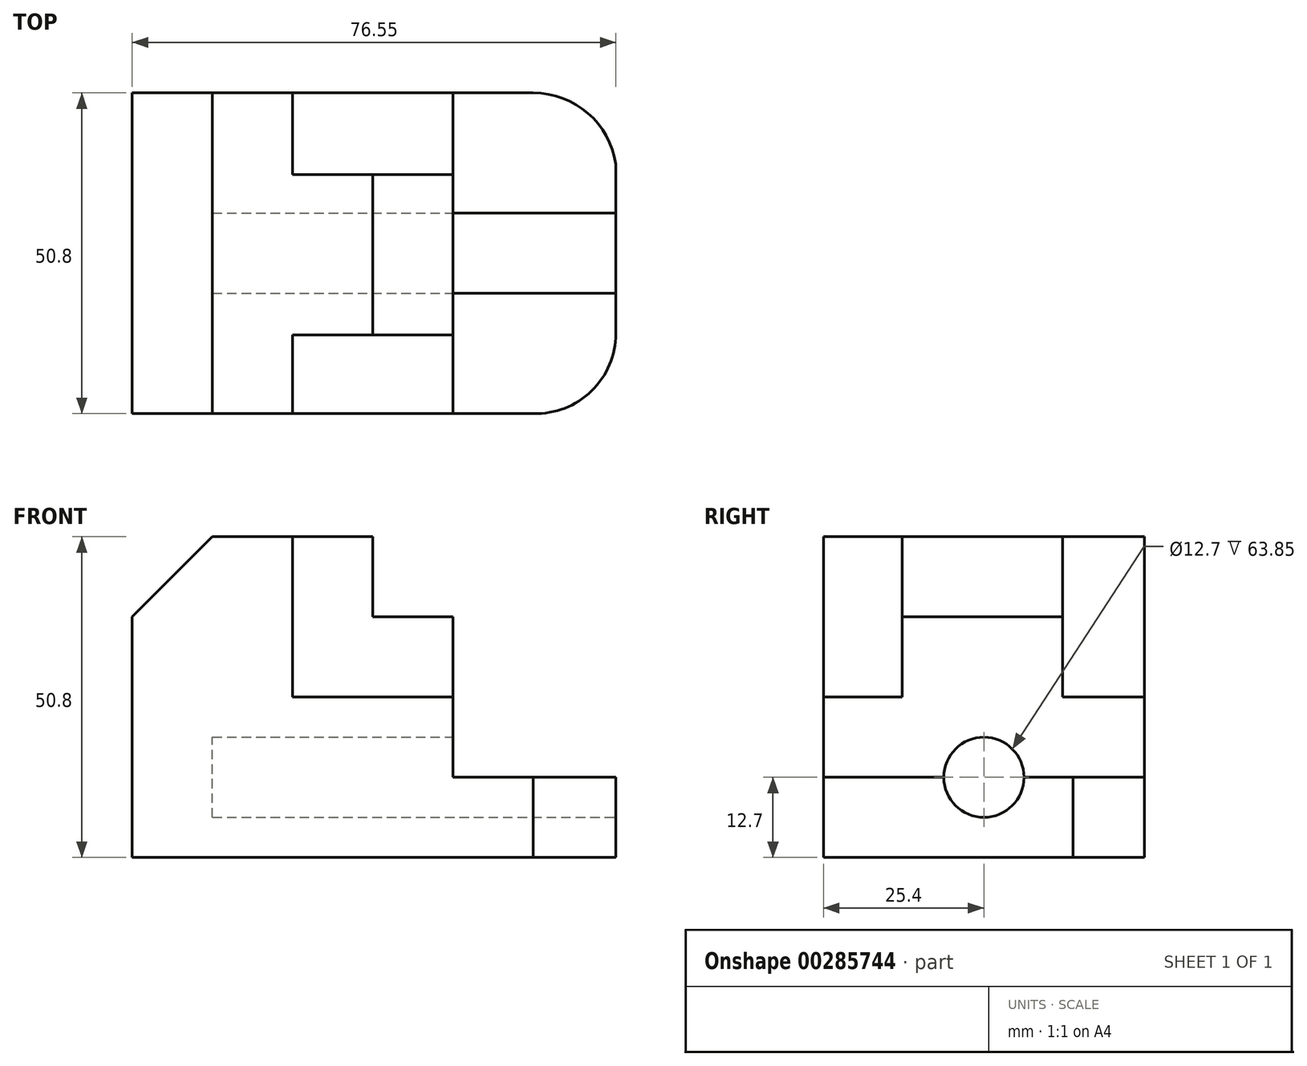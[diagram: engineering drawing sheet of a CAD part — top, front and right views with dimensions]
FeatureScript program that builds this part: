
annotation { "Feature Type Name" : "Feature", "Feature Type Description" : "" }
export const myFeature = defineFeature(function(context is Context, id is Id, definition is map)
    precondition{}
    {
        {
            var Q0;
            Q0=qCreatedBy(makeId("Front.planeOp"),FACE);
            var sketch = newSketch(context, id + "F0", { "sketchPlane" : qUnion([Q0])});
            skLineSegment(sketch, "E0", {"start": v(0, 0) * mm, "end": v(63.5, 0) * mm});
            skLineSegment(sketch, "E1", {"start": v(63.5, 0) * mm, "end": v(63.5, 12.7) * mm});
            skLineSegment(sketch, "E2", {"start": v(63.5, 12.7) * mm, "end": v(0, 12.7) * mm});
            skLineSegment(sketch, "E3", {"start": v(0, 12.7) * mm, "end": v(0, 0) * mm});
            skSolve(sketch);
        }
        {
            var Q0;
            Q0 = qSketchRegion(id + "F0", true);
            extrude(context, id + "F1", {"entities" : qUnion([Q0]), "depth" : 50.8 * mm});
        }
        {
            var Q0;
            Q0=makeQuery(id+"F1.opExtrude","CAP_FACE",FACE,{"disambiguationData":[OSD([sQuery(id+"F0.wireOp",EDGE,"E0"),sQuery(id+"F0.wireOp",EDGE,"E1"),sQuery(id+"F0.wireOp",EDGE,"E2"),sQuery(id+"F0.wireOp",EDGE,"E3")])],"isStart":false});
            var sketch = newSketch(context, id + "F2", { "sketchPlane" : qUnion([Q0])});
            skLineSegment(sketch, "E4", {"start": v(0, 12.7) * mm, "end": v(50.8, 12.7) * mm});
            skLineSegment(sketch, "E5", {"start": v(50.8, 12.7) * mm, "end": v(50.8, 25.4) * mm});
            skLineSegment(sketch, "E6", {"start": v(50.8, 25.4) * mm, "end": v(0, 25.4) * mm});
            skLineSegment(sketch, "E7", {"start": v(0, 25.4) * mm, "end": v(0, 12.7) * mm});
            skSolve(sketch);
        }
        {
            var Q0;
            Q0 = qSketchRegion(id + "F2", true);
            extrude(context, id + "F3", {"entities" : qUnion([Q0]), "operationType" : NewBodyOperationType.ADD, "oppositeDirection" : true, "depth" : 50.8 * mm});
        }
        {
            var Q0;
            Q0=makeQuery(id+"F3.boolean.opBoolean","MERGE",FACE,{"derivedFrom":[makeQuery(id+"F1.opExtrude","CAP_FACE",FACE,{"disambiguationData":[OSD([sQuery(id+"F0.wireOp",EDGE,"E0"),sQuery(id+"F0.wireOp",EDGE,"E1"),sQuery(id+"F0.wireOp",EDGE,"E2"),sQuery(id+"F0.wireOp",EDGE,"E3")])],"isStart":false}),makeQuery(id+"F3.opExtrude","CAP_FACE",FACE,{"disambiguationData":[OSD([sQuery(id+"F2.wireOp",EDGE,"E4"),sQuery(id+"F2.wireOp",EDGE,"E5"),sQuery(id+"F2.wireOp",EDGE,"E6"),sQuery(id+"F2.wireOp",EDGE,"E7")])],"isStart":true})]});
            var sketch = newSketch(context, id + "F4", { "sketchPlane" : qUnion([Q0])});
            skLineSegment(sketch, "E8", {"start": v(0, 25.4) * mm, "end": v(25.4, 25.4) * mm});
            skLineSegment(sketch, "E9", {"start": v(25.4, 25.4) * mm, "end": v(25.4, 50.8) * mm});
            skLineSegment(sketch, "E10", {"start": v(25.4, 50.8) * mm, "end": v(12.65, 50.8) * mm});
            skLineSegment(sketch, "E11", {"start": v(0, 25.4) * mm, "end": v(0, 38.1) * mm});
            skLineSegment(sketch, "E12", {"start": v(0, 38.1) * mm, "end": v(12.65, 50.8) * mm});
            skSolve(sketch);
        }
        {
            var Q0;
            Q0 = qSketchRegion(id + "F4", true);
            extrude(context, id + "F5", {"entities" : qUnion([Q0]), "operationType" : NewBodyOperationType.ADD, "oppositeDirection" : true, "depth" : 50.8 * mm});
        }
        {
            var Q0;
            Q0=makeQuery(id+"F3.opExtrude","SWEPT_FACE",FACE,{"disambiguationData":[OSD([sQuery(id+"F2.wireOp",EDGE,"E6")])]});
            var sketch = newSketch(context, id + "F6", { "sketchPlane" : qUnion([Q0])});
            skLineSegment(sketch, "E13", {"start": v(50.8, -38.34) * mm, "end": v(25.4, -38.34) * mm});
            skLineSegment(sketch, "E14", {"start": v(25.4, -38.34) * mm, "end": v(25.4, -12.94) * mm});
            skLineSegment(sketch, "E15", {"start": v(25.4, -12.94) * mm, "end": v(50.8, -12.94) * mm});
            skLineSegment(sketch, "E16", {"start": v(50.8, -12.94) * mm, "end": v(50.8, -38.34) * mm});
            skSolve(sketch);
        }
        {
            var Q0;
            Q0 = qSketchRegion(id + "F6", true);
            extrude(context, id + "F7", {"entities" : qUnion([Q0]), "operationType" : NewBodyOperationType.ADD, "depth" : 12.7 * mm});
        }
        {
            var Q0;
            Q0=makeQuery(id+"F7.opExtrude","CAP_FACE",FACE,{"disambiguationData":[OSD([sQuery(id+"F6.wireOp",EDGE,"E13"),sQuery(id+"F6.wireOp",EDGE,"E14"),sQuery(id+"F6.wireOp",EDGE,"E15"),sQuery(id+"F6.wireOp",EDGE,"E16")])],"isStart":false});
            var sketch = newSketch(context, id + "F8", { "sketchPlane" : qUnion([Q0])});
            skLineSegment(sketch, "E17", {"start": v(38.1, -38.34) * mm, "end": v(25.4, -38.34) * mm});
            skLineSegment(sketch, "E18", {"start": v(25.4, -38.34) * mm, "end": v(25.4, -12.94) * mm});
            skLineSegment(sketch, "E19", {"start": v(25.4, -12.94) * mm, "end": v(38.1, -12.94) * mm});
            skLineSegment(sketch, "E20", {"start": v(38.1, -12.94) * mm, "end": v(38.1, -38.34) * mm});
            skSolve(sketch);
        }
        {
            var Q0;
            Q0 = qSketchRegion(id + "F8", true);
            extrude(context, id + "F9", {"entities" : qUnion([Q0]), "operationType" : NewBodyOperationType.ADD, "depth" : 12.7 * mm});
        }
        {
            var Q0;
            Q0=makeQuery(id+"F1.opExtrude","SWEPT_FACE",FACE,{"disambiguationData":[OSD([sQuery(id+"F0.wireOp",EDGE,"E2")])]});
            var sketch = newSketch(context, id + "F10", { "sketchPlane" : qUnion([Q0])});
            skLineSegment(sketch, "E21", {"start": v(63.5, -38.11) * mm, "end": v(76.55, -38.11) * mm});
            skLineSegment(sketch, "E22", {"start": v(76.55, -38.11) * mm, "end": v(76.55, -11.3) * mm});
            skLineSegment(sketch, "E23", {"start": v(76.55, -11.3) * mm, "end": v(63.5, -11.3) * mm});
            skLineSegment(sketch, "E24", {"start": v(63.5, -38.11) * mm, "end": v(63.5, -11.3) * mm});
            skSolve(sketch);
        }
        {
            var Q0;
            Q0 = qSketchRegion(id + "F10", true);
            extrude(context, id + "F11", {"entities" : qUnion([Q0]), "operationType" : NewBodyOperationType.ADD, "oppositeDirection" : true, "depth" : 12.7 * mm});
        }
        {
            var Q0;
            Q0=makeQuery(id+"F11.boolean.opBoolean","MERGE",FACE,{"derivedFrom":[makeQuery(id+"F1.opExtrude","SWEPT_FACE",FACE,{"disambiguationData":[OSD([sQuery(id+"F0.wireOp",EDGE,"E2")])]}),makeQuery(id+"F11.opExtrude","CAP_FACE",FACE,{"disambiguationData":[OSD([sQuery(id+"F10.wireOp",EDGE,"E21"),sQuery(id+"F10.wireOp",EDGE,"E22"),sQuery(id+"F10.wireOp",EDGE,"E23"),sQuery(id+"F10.wireOp",EDGE,"E24")])],"isStart":true})]});
            var sketch = newSketch(context, id + "F12", { "sketchPlane" : qUnion([Q0])});
            skArc(sketch, "E25", {"start": v(76.55, -11.3) * mm, "mid": v(72.13, -3.22) * mm, "end": v(63.5, 0) * mm});
            skLineSegment(sketch, "E26", {"start": v(63.5, 0) * mm, "end": v(63.5, -11.3) * mm});
            skLineSegment(sketch, "E27", {"start": v(63.5, -11.3) * mm, "end": v(76.55, -11.3) * mm});
            skSolve(sketch);
        }
        {
            var Q0;
            Q0 = qSketchRegion(id + "F12", true);
            extrude(context, id + "F13", {"entities" : qUnion([Q0]), "operationType" : NewBodyOperationType.ADD, "oppositeDirection" : true, "depth" : 12.7 * mm});
        }
        {
            var Q0;
            Q0=makeQuery(id+"F13.boolean.opBoolean","MERGE",FACE,{"derivedFrom":[makeQuery(id+"F11.boolean.opBoolean","MERGE",FACE,{"derivedFrom":[makeQuery(id+"F1.opExtrude","SWEPT_FACE",FACE,{"disambiguationData":[OSD([sQuery(id+"F0.wireOp",EDGE,"E2")])]}),makeQuery(id+"F11.opExtrude","CAP_FACE",FACE,{"disambiguationData":[OSD([sQuery(id+"F10.wireOp",EDGE,"E21"),sQuery(id+"F10.wireOp",EDGE,"E22"),sQuery(id+"F10.wireOp",EDGE,"E23"),sQuery(id+"F10.wireOp",EDGE,"E24")])],"isStart":true})]}),makeQuery(id+"F13.opExtrude","CAP_FACE",FACE,{"disambiguationData":[OSD([sQuery(id+"F12.wireOp",EDGE,"E25"),sQuery(id+"F12.wireOp",EDGE,"E26"),sQuery(id+"F12.wireOp",EDGE,"E27")])],"isStart":true})]});
            var sketch = newSketch(context, id + "F14", { "sketchPlane" : qUnion([Q0])});
            skArc(sketch, "E28", {"start": v(63.5, -50.8) * mm, "mid": v(72.7, -47.2) * mm, "end": v(76.55, -38.11) * mm});
            skLineSegment(sketch, "E29", {"start": v(76.55, -38.11) * mm, "end": v(63.5, -38.11) * mm});
            skLineSegment(sketch, "E30", {"start": v(63.5, -38.11) * mm, "end": v(63.5, -50.8) * mm});
            skSolve(sketch);
        }
        {
            var Q0;
            Q0 = qSketchRegion(id + "F14", true);
            extrude(context, id + "F15", {"entities" : qUnion([Q0]), "operationType" : NewBodyOperationType.ADD, "oppositeDirection" : true, "depth" : 12.7 * mm});
        }
        {
            var Q0;
            Q0=makeQuery(id+"F7.boolean.opBoolean","MERGE",FACE,{"derivedFrom":[makeQuery(id+"F3.opExtrude","SWEPT_FACE",FACE,{"disambiguationData":[OSD([sQuery(id+"F2.wireOp",EDGE,"E5")])]}),makeQuery(id+"F7.opExtrude","SWEPT_FACE",FACE,{"disambiguationData":[OSD([sQuery(id+"F6.wireOp",EDGE,"E16")])]})]});
            var sketch = newSketch(context, id + "F16", { "sketchPlane" : qUnion([Q0])});
            skCircle(sketch, "E31", {"center": v(-25.4, 12.7) * mm, "radius": 6.35 * mm});
            skPoint(sketch, "E31.perimeterSnap0", {"position": v(-25.4, 12.7) * mm});
            skPoint(sketch, "E31.perimeterSnap1", {"position": v(0, 19.05) * mm});
            skSolve(sketch);
        }
        {
            var Q0;
            Q0 = qSketchRegion(id + "F16", true);
            extrude(context, id + "F17", {"entities" : qUnion([Q0]), "operationType" : NewBodyOperationType.REMOVE, "endBound" : BoundingType.SYMMETRIC, "oppositeDirection" : true, "depth" : 76.2 * mm});
        }
    });
